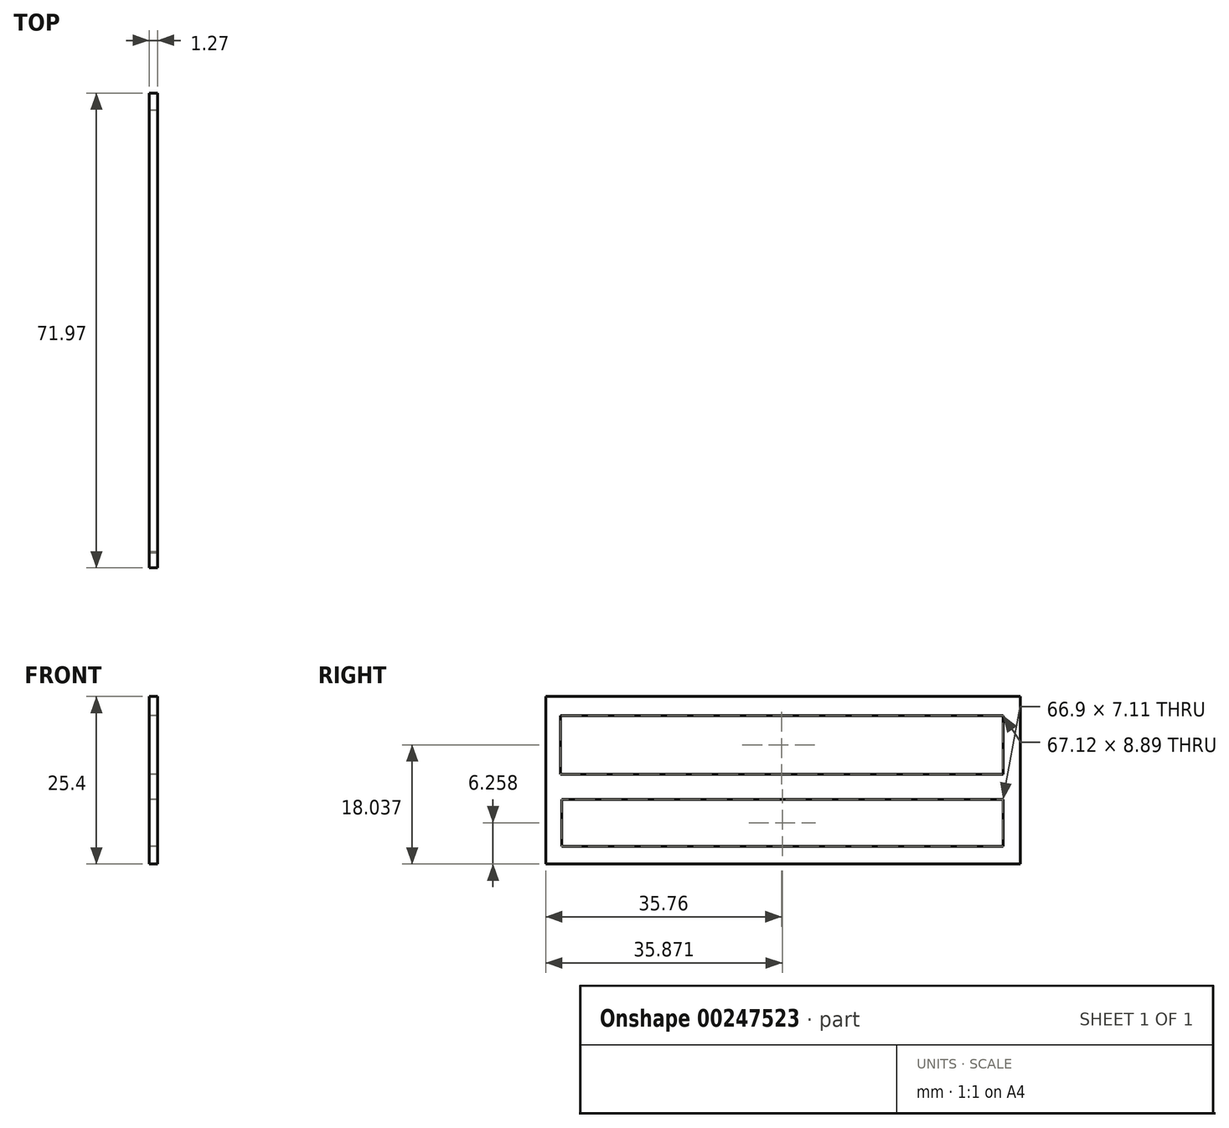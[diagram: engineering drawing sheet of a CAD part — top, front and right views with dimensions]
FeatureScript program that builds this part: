
annotation { "Feature Type Name" : "Feature", "Feature Type Description" : "" }
export const myFeature = defineFeature(function(context is Context, id is Id, definition is map)
    precondition{}
    {
        {
            var Q0;
            Q0=qCreatedBy(makeId("Right.planeOp"),FACE);
            var sketch = newSketch(context, id + "F0", { "sketchPlane" : qUnion([Q0])});
            skLineSegment(sketch, "E0.bottom", {"start": v(-69.32, 47.6) * mm, "end": v(2.65, 47.6) * mm});
            skLineSegment(sketch, "E0.top", {"start": v(-69.32, 22.2) * mm, "end": v(2.65, 22.2) * mm});
            skLineSegment(sketch, "E0.left", {"start": v(-69.32, 47.6) * mm, "end": v(-69.32, 22.2) * mm});
            skLineSegment(sketch, "E0.right", {"start": v(2.65, 47.6) * mm, "end": v(2.65, 22.2) * mm});
            skLineSegment(sketch, "E1.bottom", {"start": v(-67.12, 44.67) * mm, "end": v(0, 44.67) * mm});
            skLineSegment(sketch, "E1.top", {"start": v(-67.12, 35.78) * mm, "end": v(0, 35.78) * mm});
            skLineSegment(sketch, "E1.left", {"start": v(-67.12, 44.67) * mm, "end": v(-67.12, 35.78) * mm});
            skLineSegment(sketch, "E1.right", {"start": v(0, 44.67) * mm, "end": v(0, 35.78) * mm});
            skLineSegment(sketch, "E2.bottom", {"start": v(0, 32) * mm, "end": v(-66.9, 32) * mm});
            skLineSegment(sketch, "E2.top", {"start": v(0, 24.9) * mm, "end": v(-66.9, 24.9) * mm});
            skLineSegment(sketch, "E2.left", {"start": v(0, 32) * mm, "end": v(0, 24.9) * mm});
            skLineSegment(sketch, "E2.right", {"start": v(-66.9, 32) * mm, "end": v(-66.9, 24.9) * mm});
            skSolve(sketch);
        }
        {
            var Q0;
            Q0 = qSketchRegion(id + "F0", true);
            extrude(context, id + "F1", {"entities" : qUnion([Q0]), "depth" : 1.27 * mm});
        }
    });
